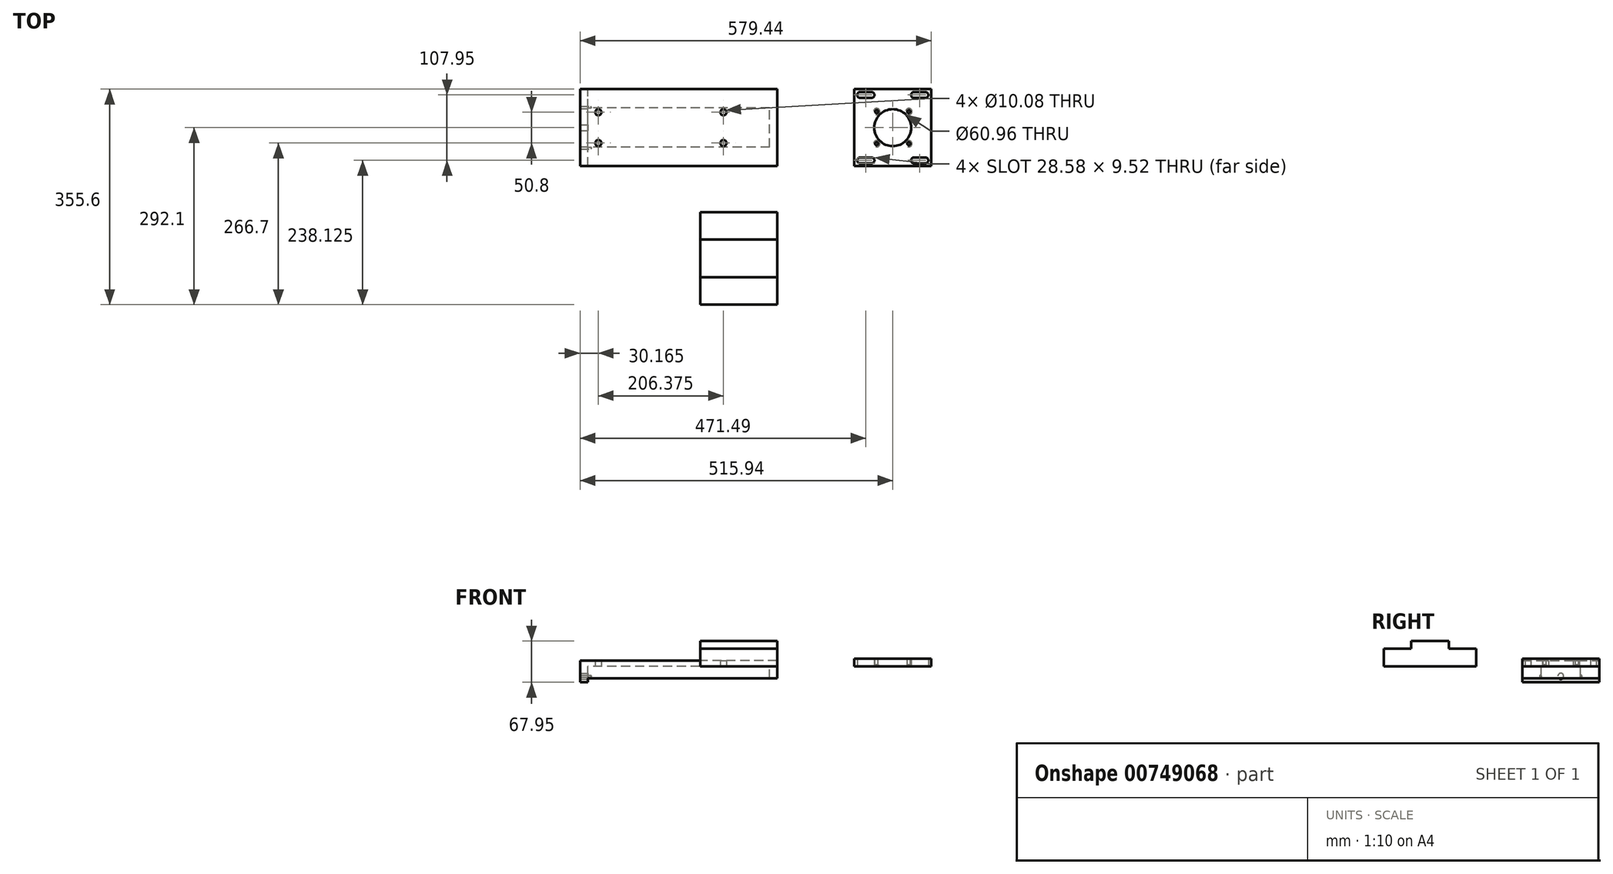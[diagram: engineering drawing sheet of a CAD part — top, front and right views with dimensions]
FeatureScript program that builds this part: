
annotation { "Feature Type Name" : "Feature", "Feature Type Description" : "" }
export const myFeature = defineFeature(function(context is Context, id is Id, definition is map)
    precondition{}
    {
        {
            var Q0;
            Q0=qCreatedBy(makeId("Top.planeOp"),FACE);
            var sketch = newSketch(context, id + "F0", { "sketchPlane" : qUnion([Q0])});
            skLineSegment(sketch, "E0.bottom", {"start": v(0, 0) * mm, "end": v(-325.44, 0) * mm});
            skLineSegment(sketch, "E0.top", {"start": v(0, 127) * mm, "end": v(-325.44, 127) * mm});
            skLineSegment(sketch, "E0.left", {"start": v(0, 0) * mm, "end": v(0, 127) * mm});
            skLineSegment(sketch, "E0.right", {"start": v(-325.44, 0) * mm, "end": v(-325.44, 127) * mm});
            skSolve(sketch);
        }
        {
            var Q0;
            Q0 = qSketchRegion(id + "F0", true);
            extrude(context, id + "F1", {"entities" : qUnion([Q0]), "depth" : 9.52 * mm, "offsetDistance" : 25.4 * mm});
        }
        {
            var Q0;
            Q0=makeQuery(id+"F1.opExtrude","CAP_FACE",FACE,{"disambiguationData":[OSD([sQuery(id+"F0.wireOp",EDGE,"E0.bottom"),sQuery(id+"F0.wireOp",EDGE,"E0.top"),sQuery(id+"F0.wireOp",EDGE,"E0.left"),sQuery(id+"F0.wireOp",EDGE,"E0.right")])],"isStart":true});
            var sketch = newSketch(context, id + "F2", { "sketchPlane" : qUnion([Q0])});
            skLineSegment(sketch, "E1.bottom", {"start": v(-325.44, 0) * mm, "end": v(-312.74, 0) * mm});
            skLineSegment(sketch, "E1.top", {"start": v(-325.44, -127) * mm, "end": v(-312.74, -127) * mm});
            skLineSegment(sketch, "E1.left", {"start": v(-325.44, 0) * mm, "end": v(-325.44, -127) * mm});
            skLineSegment(sketch, "E1.right", {"start": v(-312.74, -31.12) * mm, "end": v(-312.74, -95.88) * mm});
            skLineSegment(sketch, "E2.bottom", {"start": v(0, 0) * mm, "end": v(-12.7, 0) * mm});
            skLineSegment(sketch, "E2.top", {"start": v(0, -127) * mm, "end": v(-12.7, -127) * mm});
            skLineSegment(sketch, "E2.left", {"start": v(0, 0) * mm, "end": v(0, -127) * mm});
            skLineSegment(sketch, "E2.right", {"start": v(-12.7, -31.11) * mm, "end": v(-12.7, -95.89) * mm});
            skLineSegment(sketch, "E3", {"start": v(0, -63.5) * mm, "end": v(-325.44, -63.5) * mm, "construction": true});
            skLineSegment(sketch, "E4.bottom", {"start": v(-12.7, -31.11) * mm, "end": v(-312.74, -31.12) * mm});
            skLineSegment(sketch, "E4.top", {"start": v(-12.7, 0) * mm, "end": v(-312.74, 0) * mm});
            skLineSegment(sketch, "E5.MirrorCS", {"start": v(-12.7, -95.89) * mm, "end": v(-312.74, -95.88) * mm});
            skLineSegment(sketch, "E6.MirrorCS", {"start": v(-12.7, -127) * mm, "end": v(-312.74, -127) * mm});
            skLineSegment(sketch, "E7", {"start": v(-312.74, 0) * mm, "end": v(-312.74, -31.12) * mm});
            skLineSegment(sketch, "E8", {"start": v(-312.74, -95.88) * mm, "end": v(-312.74, -127) * mm});
            skLineSegment(sketch, "E9", {"start": v(-12.7, -31.11) * mm, "end": v(-12.7, 0) * mm});
            skSolve(sketch);
        }
        {
            var Q0;
            Q0 = qSketchRegion(id + "F2", true);
            extrude(context, id + "F3", {"entities" : qUnion([Q0]), "operationType" : NewBodyOperationType.ADD, "depth" : 19.68 * mm, "offsetDistance" : 25.4 * mm});
        }
        {
            var Q0;
            Q0=makeQuery(id+"F3.boolean.opBoolean","MERGE",FACE,{"derivedFrom":[makeQuery(id+"F1.opExtrude","SWEPT_FACE",FACE,{"disambiguationData":[OSD([sQuery(id+"F0.wireOp",EDGE,"E0.right")])]}),makeQuery(id+"F3.opExtrude","SWEPT_FACE",FACE,{"disambiguationData":[OSD([sQuery(id+"F2.wireOp",EDGE,"E1.left")])]})]});
            var sketch = newSketch(context, id + "F4", { "sketchPlane" : qUnion([Q0])});
            skPoint(sketch, "E10", {"position": v(-63.5, -15.88) * mm});
            skPoint(sketch, "E10.positionSnap0", {"position": v(-63.5, -19.69) * mm});
            skSolve(sketch);
        }
        {
            var Q0;
            Q0=qCreatedBy(makeId("Top.planeOp"),FACE);
            var sketch = newSketch(context, id + "F5", { "sketchPlane" : qUnion([Q0])});
            skLineSegment(sketch, "E11.bottom", {"start": v(0, -228.6) * mm, "end": v(-127, -228.6) * mm});
            skLineSegment(sketch, "E11.top", {"start": v(0, -76.2) * mm, "end": v(-127, -76.2) * mm});
            skLineSegment(sketch, "E11.left", {"start": v(0, -228.6) * mm, "end": v(0, -76.2) * mm});
            skLineSegment(sketch, "E11.right", {"start": v(-127, -228.6) * mm, "end": v(-127, -76.2) * mm});
            skSolve(sketch);
        }
        {
            var Q0;
            Q0 = qSketchRegion(id + "F5", true);
            extrude(context, id + "F6", {"entities" : qUnion([Q0]), "depth" : 29.2 * mm, "offsetDistance" : 25.4 * mm});
        }
        {
            var Q0;
            Q0=makeQuery(id+"F3.opExtrude","CAP_FACE",FACE,{"disambiguationData":[OSD([sQuery(id+"F2.wireOp",EDGE,"E1.bottom"),sQuery(id+"F2.wireOp",EDGE,"E1.top"),sQuery(id+"F2.wireOp",EDGE,"E1.left"),sQuery(id+"F2.wireOp",EDGE,"E1.right"),sQuery(id+"F2.wireOp",EDGE,"E2.bottom"),sQuery(id+"F2.wireOp",EDGE,"E2.top"),sQuery(id+"F2.wireOp",EDGE,"E2.left"),sQuery(id+"F2.wireOp",EDGE,"E2.right"),sQuery(id+"F2.wireOp",EDGE,"E4.bottom"),sQuery(id+"F2.wireOp",EDGE,"E4.top"),sQuery(id+"F2.wireOp",EDGE,"E5.MirrorCS"),sQuery(id+"F2.wireOp",EDGE,"E6.MirrorCS")])],"isStart":false});
            var sketch = newSketch(context, id + "F7", { "sketchPlane" : qUnion([Q0])});
            skPoint(sketch, "E12.oppositeSnap0", {"position": v(-325.44, -63.5) * mm});
            skLineSegment(sketch, "E13.bottom", {"start": v(-325.44, -127) * mm, "end": v(-312.74, -127) * mm});
            skLineSegment(sketch, "E13.top", {"start": v(-325.44, 0) * mm, "end": v(-312.74, 0) * mm});
            skLineSegment(sketch, "E13.left", {"start": v(-325.44, -127) * mm, "end": v(-325.44, 0) * mm});
            skLineSegment(sketch, "E13.right", {"start": v(-312.74, -127) * mm, "end": v(-312.74, 0) * mm});
            skSolve(sketch);
        }
        {
            var Q0;
            Q0 = qSketchRegion(id + "F7", true);
            extrude(context, id + "F8", {"entities" : qUnion([Q0]), "operationType" : NewBodyOperationType.ADD, "depth" : 6.35 * mm, "offsetDistance" : 25.4 * mm});
        }
        {
            var Q0;
            Q0=sQuery(id+"F4.wireOp",VERTEX,"E10");
            var Q1;
            Q1=makeQuery(id+"F1.opExtrude","SWEPT_BODY",BODY,{"disambiguationData":[OSD([sQuery(id+"F0.wireOp",EDGE,"E0.bottom"),sQuery(id+"F0.wireOp",EDGE,"E0.top"),sQuery(id+"F0.wireOp",EDGE,"E0.left"),sQuery(id+"F0.wireOp",EDGE,"E0.right")])]});
            hole(context, id + "F9", {"style" : HoleStyle.SIMPLE, "endStyle" : HoleEndStyle.BLIND, "holeDiameter" : 9.52 * mm, "majorDiameter" : 6.35 * mm, "holeDepth" : 12.7 * mm, "isTappedThrough" : true, "tappedDepth" : 7.42 * mm, "tapClearance" : 3, "locations" : qUnion([Q0]), "scope" : qUnion([Q1])});
        }
        {
            var Q0;
            Q0=makeQuery(id+"F6.opExtrude","CAP_FACE",FACE,{"disambiguationData":[OSD([sQuery(id+"F5.wireOp",EDGE,"E11.bottom"),sQuery(id+"F5.wireOp",EDGE,"E11.top"),sQuery(id+"F5.wireOp",EDGE,"E11.left"),sQuery(id+"F5.wireOp",EDGE,"E11.right")])],"isStart":false});
            var sketch = newSketch(context, id + "F10", { "sketchPlane" : qUnion([Q0])});
            skLineSegment(sketch, "E14.top", {"start": v(-127, -183.52) * mm, "end": v(0, -183.52) * mm});
            skLineSegment(sketch, "E14.left", {"start": v(-127, -152.4) * mm, "end": v(-127, -183.52) * mm});
            skLineSegment(sketch, "E14.right", {"start": v(0, -152.4) * mm, "end": v(0, -183.52) * mm});
            skLineSegment(sketch, "E15.MirrorCS", {"start": v(-127, -121.29) * mm, "end": v(0, -121.29) * mm});
            skLineSegment(sketch, "E16.MirrorCS", {"start": v(-127, -152.4) * mm, "end": v(-127, -121.29) * mm});
            skLineSegment(sketch, "E17.MirrorCS", {"start": v(0, -152.4) * mm, "end": v(0, -121.29) * mm});
            skSolve(sketch);
        }
        {
            var Q0;
            Q0 = qSketchRegion(id + "F10", true);
            extrude(context, id + "F11", {"entities" : qUnion([Q0]), "operationType" : NewBodyOperationType.ADD, "depth" : 12.7 * mm, "offsetDistance" : 25.4 * mm});
        }
        {
            var Q0;
            Q0=qCreatedBy(makeId("Top.planeOp"),FACE);
            var sketch = newSketch(context, id + "F12", { "sketchPlane" : qUnion([Q0])});
            skLineSegment(sketch, "E18.bottom", {"start": v(254, 0) * mm, "end": v(127, 0) * mm});
            skLineSegment(sketch, "E18.top", {"start": v(254, 127) * mm, "end": v(127, 127) * mm});
            skLineSegment(sketch, "E18.left", {"start": v(254, 0) * mm, "end": v(254, 127) * mm});
            skLineSegment(sketch, "E18.right", {"start": v(127, 0) * mm, "end": v(127, 127) * mm});
            skLineSegment(sketch, "E19", {"start": v(190.5, 0) * mm, "end": v(190.5, 127) * mm, "construction": true});
            skLineSegment(sketch, "E20", {"start": v(127, 63.5) * mm, "end": v(254, 63.5) * mm, "construction": true});
            skLineSegment(sketch, "E21.bottom", {"start": v(154.5, 99.5) * mm, "end": v(226.5, 99.5) * mm, "construction": true});
            skLineSegment(sketch, "E21.top", {"start": v(154.5, 27.5) * mm, "end": v(226.5, 27.5) * mm, "construction": true});
            skLineSegment(sketch, "E21.left", {"start": v(154.5, 99.5) * mm, "end": v(154.5, 27.5) * mm, "construction": true});
            skLineSegment(sketch, "E21.right", {"start": v(226.5, 99.5) * mm, "end": v(226.5, 27.5) * mm, "construction": true});
            skPoint(sketch, "E21.middle", {"position": v(190.5, 63.5) * mm});
            skCircle(sketch, "E22", {"center": v(190.5, 63.5) * mm, "radius": 30.48 * mm});
            skCircle(sketch, "E23", {"center": v(190.5, 63.5) * mm, "radius": 37.5 * mm, "construction": true});
            skLineSegment(sketch, "E24", {"start": v(190.5, 63.5) * mm, "end": v(154.5, 99.5) * mm, "construction": true});
            skPoint(sketch, "E25", {"position": v(163.98, 90.02) * mm});
            skPoint(sketch, "E26.MirrorP", {"position": v(163.98, 36.98) * mm});
            skPoint(sketch, "E27.MirrorP", {"position": v(217.02, 36.98) * mm});
            skPoint(sketch, "E28.MirrorP", {"position": v(217.02, 90.02) * mm});
            skLineSegment(sketch, "E29", {"start": v(127, 117.47) * mm, "end": v(254, 117.47) * mm, "construction": true});
            skArc(sketch, "E30", {"start": v(136.53, 122.24) * mm, "mid": v(131.76, 117.47) * mm, "end": v(136.53, 112.71) * mm});
            skArc(sketch, "E31", {"start": v(155.58, 112.71) * mm, "mid": v(160.34, 117.47) * mm, "end": v(155.58, 122.24) * mm});
            skLineSegment(sketch, "E32", {"start": v(155.58, 122.24) * mm, "end": v(136.53, 122.24) * mm});
            skLineSegment(sketch, "E33", {"start": v(155.58, 112.71) * mm, "end": v(136.53, 112.71) * mm});
            skLineSegment(sketch, "E34.MirrorCS", {"start": v(155.58, 14.29) * mm, "end": v(136.53, 14.29) * mm});
            skArc(sketch, "E35.MirrorCS", {"start": v(136.53, 4.76) * mm, "mid": v(131.76, 9.53) * mm, "end": v(136.53, 14.29) * mm});
            skLineSegment(sketch, "E36.MirrorCS", {"start": v(155.58, 4.76) * mm, "end": v(136.53, 4.76) * mm});
            skArc(sketch, "E37.MirrorCS", {"start": v(155.58, 14.29) * mm, "mid": v(160.34, 9.53) * mm, "end": v(155.58, 4.76) * mm});
            skLineSegment(sketch, "E38.MirrorCS", {"start": v(225.42, 112.71) * mm, "end": v(244.47, 112.71) * mm});
            skLineSegment(sketch, "E39.MirrorCS", {"start": v(225.43, 122.24) * mm, "end": v(244.48, 122.24) * mm});
            skArc(sketch, "E40.MirrorCS", {"start": v(225.43, 112.71) * mm, "mid": v(220.66, 117.47) * mm, "end": v(225.43, 122.24) * mm});
            skArc(sketch, "E41.MirrorCS", {"start": v(244.48, 122.24) * mm, "mid": v(249.24, 117.47) * mm, "end": v(244.48, 112.71) * mm});
            skArc(sketch, "E42.MirrorCS", {"start": v(244.47, 4.76) * mm, "mid": v(249.24, 9.53) * mm, "end": v(244.47, 14.29) * mm});
            skLineSegment(sketch, "E43.MirrorCS", {"start": v(225.42, 14.29) * mm, "end": v(244.47, 14.29) * mm});
            skLineSegment(sketch, "E44.MirrorCS", {"start": v(225.42, 4.76) * mm, "end": v(244.47, 4.76) * mm});
            skArc(sketch, "E45.MirrorCS", {"start": v(225.42, 14.29) * mm, "mid": v(220.66, 9.53) * mm, "end": v(225.42, 4.76) * mm});
            skSolve(sketch);
        }
        {
            var Q0;
            Q0 = qSketchRegion(id + "F12", true);
            extrude(context, id + "F13", {"entities" : qUnion([Q0]), "depth" : 12.7 * mm, "offsetDistance" : 25.4 * mm});
        }
        {
            var Q0;
            Q0=sQuery(id+"F12.wireOp",VERTEX,"E27.MirrorP");
            var Q1;
            Q1=sQuery(id+"F12.wireOp",VERTEX,"E28.MirrorP");
            var Q2;
            Q2=sQuery(id+"F12.wireOp",VERTEX,"E25");
            var Q3;
            Q3=sQuery(id+"F12.wireOp",VERTEX,"E26.MirrorP");
            var Q4;
            Q4=makeQuery(id+"F13.opExtrude","SWEPT_BODY",BODY,{"disambiguationData":[OSD([sQuery(id+"F12.wireOp",EDGE,"E18.bottom"),sQuery(id+"F12.wireOp",EDGE,"E18.top"),sQuery(id+"F12.wireOp",EDGE,"E18.left"),sQuery(id+"F12.wireOp",EDGE,"E18.right"),sQuery(id+"F12.wireOp",EDGE,"wSka1kYB-u1eB-SOg9-Qxg8-Cg5vfJebmHGo"),sQuery(id+"F12.wireOp",EDGE,"rV8CMpv5-dqZh-jyjk-fxgw-ndZA5UFrruDB"),sQuery(id+"F12.wireOp",EDGE,"b32a5068-e048-486b-ae29-734e139f8fcf0.MirrorC"),sQuery(id+"F12.wireOp",EDGE,"dd3dcb2d-bbd5-4889-98b1-f2bc5e725b570.MirrorC"),sQuery(id+"F12.wireOp",EDGE,"TbdLZrST-BNm8-BwNX-zX1D-SX8P2FHjafpP"),sQuery(id+"F12.wireOp",EDGE,"QipHP4tf-wjmz-43Bb-BCgt-74qcTD9Wdp96"),sQuery(id+"F12.wireOp",EDGE,"pHRHV3rf-To4n-bGLz-vhrW-SSDTvrdckNBt"),sQuery(id+"F12.wireOp",EDGE,"gmA40VZ4-YtV6-qXK0-EhWk-411Fcp1WO4Bt"),sQuery(id+"F12.wireOp",EDGE,"dcb78208-4069-40bf-8891-e9afc4e31fd20.MirrorCS"),sQuery(id+"F12.wireOp",EDGE,"2032dcb5-6bba-4c86-9265-02d0f9ae6bdf0.MirrorCS"),sQuery(id+"F12.wireOp",EDGE,"b87bfd5d-d777-4172-afd7-86f24dd4adf20.MirrorCS"),sQuery(id+"F12.wireOp",EDGE,"1dec0e3b-ec7a-463c-8044-fe5185e101220.MirrorCS"),sQuery(id+"F12.wireOp",EDGE,"85c5250d-04fa-497e-9aad-99babd6891dd0.MirrorCS"),sQuery(id+"F12.wireOp",EDGE,"d9d88fc1-2d97-45e3-ae69-2fab431306310.MirrorCS"),sQuery(id+"F12.wireOp",EDGE,"2e93608c-420d-4b3d-a1f3-53d68fb3de870.MirrorCS"),sQuery(id+"F12.wireOp",EDGE,"9741a420-1130-40a3-97b4-1db8a66139ab0.MirrorCS"),sQuery(id+"F12.wireOp",EDGE,"E22")])]});
            hole(context, id + "F14", {"style" : HoleStyle.C_SINK, "endStyle" : HoleEndStyle.BLIND, "oppositeDirection" : true, "standardTappedOrClearance" : lookupTablePath({ "standard" : "ANSI", "fit" : "Normal (ASME)", "size" : "#10", "type" : "Clearance" }), "standardBlindInLast" : lookupTablePath({ "fit" : "Free", "standard" : "ANSI", "size" : "#10", "type" : "Clearance" }), "holeDiameter" : 5.1 * mm, "cSinkDiameter" : 10.44 * mm, "cSinkAngle" : 82 * degree, "majorDiameter" : 6.35 * mm, "holeDepth" : 15.88 * mm, "isTappedThrough" : true, "tappedDepth" : 7.42 * mm, "tapClearance" : 3, "locations" : qUnion([Q0, Q1, Q2, Q3]), "scope" : qUnion([Q4])});
        }
        {
            var Q0;
            Q0=makeQuery(id+"F8.boolean.opBoolean","MERGE",FACE,{"derivedFrom":[makeQuery(id+"F3.boolean.opBoolean","MERGE",FACE,{"derivedFrom":[makeQuery(id+"F1.opExtrude","SWEPT_FACE",FACE,{"disambiguationData":[OSD([sQuery(id+"F0.wireOp",EDGE,"E0.right")])]}),makeQuery(id+"F3.opExtrude","SWEPT_FACE",FACE,{"disambiguationData":[OSD([sQuery(id+"F2.wireOp",EDGE,"E1.left")])]})]}),makeQuery(id+"F8.opExtrude","SWEPT_FACE",FACE,{"disambiguationData":[OSD([sQuery(id+"F7.wireOp",EDGE,"E12.right")])]})]});
            var sketch = newSketch(context, id + "F15", { "sketchPlane" : qUnion([Q0])});
            skLineSegment(sketch, "E46", {"start": v(-127, -15.88) * mm, "end": v(0, -15.87) * mm, "construction": true});
            skLineSegment(sketch, "E47", {"start": v(-63.5, 9.53) * mm, "end": v(-63.5, -26.04) * mm, "construction": true});
            skPoint(sketch, "E48", {"position": v(-30.16, -15.87) * mm});
            skPoint(sketch, "E49.MirrorP", {"position": v(-96.84, -15.88) * mm});
            skSolve(sketch);
        }
        {
            var Q0;
            Q0=sQuery(id+"F15.wireOp",VERTEX,"E48");
            var Q1;
            Q1=sQuery(id+"F15.wireOp",VERTEX,"E49.MirrorP");
            var Q2;
            Q2=makeQuery(id+"F1.opExtrude","SWEPT_BODY",BODY,{"disambiguationData":[OSD([sQuery(id+"F0.wireOp",EDGE,"E0.bottom"),sQuery(id+"F0.wireOp",EDGE,"E0.top"),sQuery(id+"F0.wireOp",EDGE,"E0.left"),sQuery(id+"F0.wireOp",EDGE,"E0.right")])]});
            hole(context, id + "F16", {"style" : HoleStyle.SIMPLE, "endStyle" : HoleEndStyle.BLIND, "standardTappedOrClearance" : lookupTablePath({ "standard" : "ISO", "engagement" : "75%", "pitch" : "0.7 mm", "size" : "M4", "type" : "Tapped" }), "standardBlindInLast" : lookupTablePath({ "standard" : "ISO", "engagement" : "75%", "pitch" : "0.7 mm", "size" : "M4", "type" : "Tapped" }), "holeDiameter" : 3.3 * mm, "majorDiameter" : 4 * mm, "showTappedDepth" : true, "holeDepth" : 17.97 * mm, "isTappedThrough" : true, "tappedDepth" : 15.88 * mm, "tapClearance" : 3, "locations" : qUnion([Q0, Q1]), "scope" : qUnion([Q2])});
        }
        {
            var Q0;
            Q0=makeQuery(id+"F1.opExtrude","CAP_FACE",FACE,{"disambiguationData":[OSD([sQuery(id+"F0.wireOp",EDGE,"E0.bottom"),sQuery(id+"F0.wireOp",EDGE,"E0.top"),sQuery(id+"F0.wireOp",EDGE,"E0.left"),sQuery(id+"F0.wireOp",EDGE,"E0.right")])],"isStart":false});
            var sketch = newSketch(context, id + "F17", { "sketchPlane" : qUnion([Q0])});
            skLineSegment(sketch, "E50.0", {"start": v(0, 0) * mm, "end": v(-325.44, 0) * mm, "construction": true});
            skLineSegment(sketch, "E51.0", {"start": v(-325.44, 0) * mm, "end": v(-325.44, 127) * mm, "construction": true});
            skLineSegment(sketch, "E52", {"start": v(-162.72, 0) * mm, "end": v(-162.72, 127) * mm, "construction": true});
            skLineSegment(sketch, "E53", {"start": v(-325.44, 63.5) * mm, "end": v(0, 63.5) * mm, "construction": true});
            skLineSegment(sketch, "E54", {"start": v(-295.28, 0) * mm, "end": v(-295.28, 127) * mm, "construction": true});
            skLineSegment(sketch, "E55", {"start": v(-88.9, 0) * mm, "end": v(-88.9, 127) * mm, "construction": true});
            skPoint(sketch, "E56", {"position": v(-295.28, 38.1) * mm});
            skPoint(sketch, "E57.MirrorP", {"position": v(-295.28, 88.9) * mm});
            skPoint(sketch, "E58", {"position": v(-88.9, 38.1) * mm});
            skPoint(sketch, "E59.MirrorP", {"position": v(-88.9, 88.9) * mm});
            skSolve(sketch);
        }
        {
            var Q0;
            Q0=sQuery(id+"F17.wireOp",VERTEX,"E56");
            var Q1;
            Q1=sQuery(id+"F17.wireOp",VERTEX,"E57.MirrorP");
            var Q2;
            Q2=sQuery(id+"F17.wireOp",VERTEX,"E58");
            var Q3;
            Q3=sQuery(id+"F17.wireOp",VERTEX,"E59.MirrorP");
            var Q4;
            Q4=makeQuery(id+"F1.opExtrude","SWEPT_BODY",BODY,{"disambiguationData":[OSD([sQuery(id+"F0.wireOp",EDGE,"E0.bottom"),sQuery(id+"F0.wireOp",EDGE,"E0.top"),sQuery(id+"F0.wireOp",EDGE,"E0.left"),sQuery(id+"F0.wireOp",EDGE,"E0.right")])]});
            hole(context, id + "F18", {"style" : HoleStyle.SIMPLE, "endStyle" : HoleEndStyle.BLIND, "standardTappedOrClearance" : lookupTablePath({ "standard" : "ANSI", "fit" : "Normal (ASME)", "size" : "3/8", "type" : "Clearance" }), "standardBlindInLast" : lookupTablePath({ "fit" : "Free", "standard" : "ANSI", "size" : "3/8", "type" : "Clearance" }), "holeDiameter" : 10.08 * mm, "majorDiameter" : 6.35 * mm, "holeDepth" : 20.62 * mm, "isTappedThrough" : true, "tappedDepth" : 15.88 * mm, "tapClearance" : 3, "locations" : qUnion([Q0, Q1, Q2, Q3]), "scope" : qUnion([Q4])});
        }
    });
